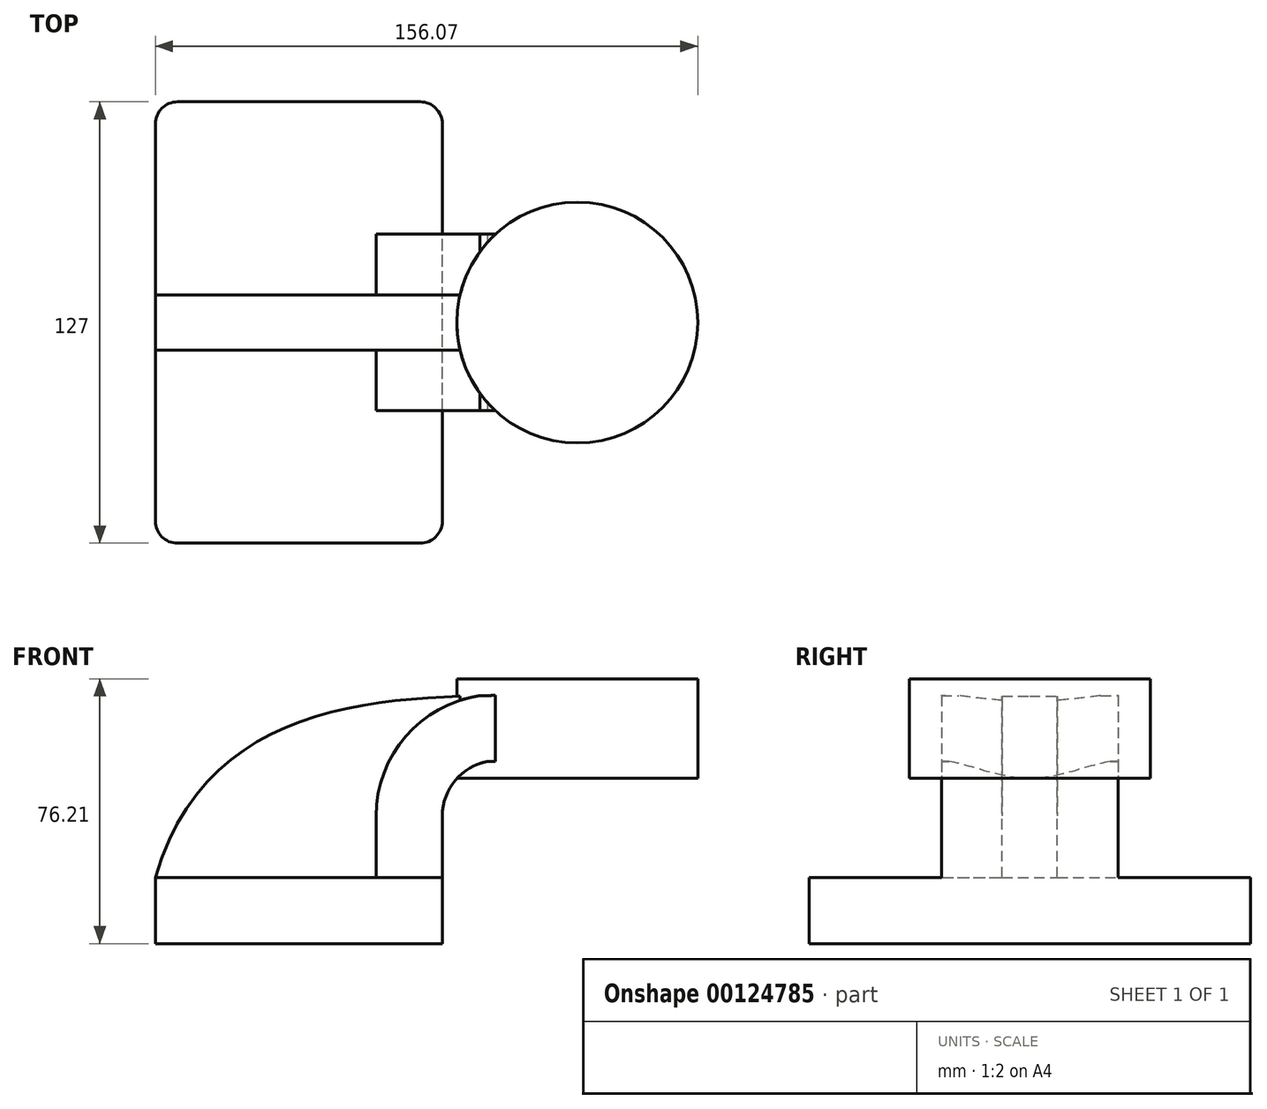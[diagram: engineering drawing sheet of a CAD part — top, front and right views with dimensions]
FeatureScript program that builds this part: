
annotation { "Feature Type Name" : "Feature", "Feature Type Description" : "" }
export const myFeature = defineFeature(function(context is Context, id is Id, definition is map)
    precondition{}
    {
        {
            var Q0;
            Q0=qCreatedBy(makeId("Front.planeOp"),FACE);
            var sketch = newSketch(context, id + "F0", { "sketchPlane" : qUnion([Q0])});
            skLineSegment(sketch, "E0.bottom", {"start": v(-41.28, 9.52) * mm, "end": v(41.28, 9.53) * mm});
            skLineSegment(sketch, "E0.top", {"start": v(-41.28, -9.53) * mm, "end": v(41.28, -9.53) * mm});
            skLineSegment(sketch, "E0.left", {"start": v(-41.28, 9.52) * mm, "end": v(-41.28, -9.53) * mm});
            skLineSegment(sketch, "E0.right", {"start": v(41.28, 9.53) * mm, "end": v(41.28, -9.52) * mm});
            skPoint(sketch, "E0.middle", {"position": v(0, 0) * mm});
            skLineSegment(sketch, "E1.bottom", {"start": v(64, 66.67) * mm, "end": v(114.8, 66.67) * mm});
            skLineSegment(sketch, "E1.top", {"start": v(64, 38.1) * mm, "end": v(114.8, 38.1) * mm});
            skLineSegment(sketch, "E1.left", {"start": v(64, 66.67) * mm, "end": v(64, 38.1) * mm});
            skLineSegment(sketch, "E1.right", {"start": v(114.8, 66.67) * mm, "end": v(114.8, 38.1) * mm});
            skPoint(sketch, "E1.middle", {"position": v(89.4, 52.39) * mm});
            skLineSegment(sketch, "E2", {"start": v(41.27, 9.53) * mm, "end": v(41.27, 27.25) * mm});
            skArc(sketch, "E3", {"start": v(41.27, 27.25) * mm, "mid": v(44.98, 37.44) * mm, "end": v(54.37, 42.88) * mm});
            skLineSegment(sketch, "E4", {"start": v(54.37, 42.88) * mm, "end": v(80.13, 42.88) * mm});
            skLineSegment(sketch, "E5.0", {"start": v(53.02, 61.93) * mm, "end": v(80.13, 61.93) * mm});
            skArc(sketch, "E5.1", {"start": v(22.22, 27.25) * mm, "mid": v(31.03, 50.43) * mm, "end": v(53.02, 61.93) * mm});
            skLineSegment(sketch, "E5.2", {"start": v(22.22, 9.53) * mm, "end": v(22.22, 27.25) * mm});
            skLineSegment(sketch, "E6", {"start": v(80.13, 38.1) * mm, "end": v(80.13, 66.67) * mm});
            skFitSpline(sketch, "E7", {"points": [v(-41.28, 9.52) * mm, v(64, 61.93) * mm], "startDerivative": vector(44.55, 155.05) * mm, "endDerivative": vector(115.8, 0.6) * mm});
            skSolve(sketch);
        }
        {
            var Q0;
            Q0=makeQuery(id+"F0.imprint","IMPRINT",FACE,{"disambiguationData":[TD([[makeQuery(id+"F0.imprint","IMPRINT",EDGE,{"derivedFrom":sQuery(id+"F0.wireOp",EDGE,"E0.top")}),1.0]])]});
            extrude(context, id + "F1", {"entities" : qUnion([Q0]), "endBound" : BoundingType.SYMMETRIC, "depth" : 127 * mm});
        }
        {
            var Q0;
            {var subQ1=sQuery(id+"F0.wireOp",EDGE,"E2");Q0=makeQuery(id+"F0.imprint","IMPRINT",FACE,{"disambiguationData":[TD([[makeQuery(id+"F0.imprint","IMPRINT",EDGE,{"derivedFrom":subQ1}),1.0]])]});}
            var Q1;
            {var subQ3=sQuery(id+"F0.wireOp",EDGE,"E4");var subQ5=sQuery(id+"F0.wireOp",EDGE,"E6");var subQ6=makeQuery(id+"F0.imprint","INTERSECT",VERTEX,{"derivedFrom":[subQ3,subQ5]});Q1=makeQuery(id+"F0.imprint","IMPRINT",FACE,{"disambiguationData":[TD([[makeQuery(id+"F0.imprint","IMPRINT",EDGE,{"disambiguationData":[TD([[subQ6,1.0]])],"derivedFrom":subQ3}),1.0]])]});}
            extrude(context, id + "F2", {"entities" : qUnion([Q0, Q1]), "operationType" : NewBodyOperationType.ADD, "endBound" : BoundingType.SYMMETRIC, "depth" : 50.8 * mm});
        }
        {
            var Q0;
            {var subQ3=sQuery(id+"F0.wireOp",EDGE,"E5.2");Q0=makeQuery(id+"F0.imprint","IMPRINT",FACE,{"disambiguationData":[TD([[makeQuery(id+"F0.imprint","IMPRINT",EDGE,{"derivedFrom":subQ3}),1.0]])]});}
            extrude(context, id + "F3", {"entities" : qUnion([Q0]), "operationType" : NewBodyOperationType.ADD, "endBound" : BoundingType.SYMMETRIC, "depth" : 15.88 * mm});
        }
        {
            var Q0;
            {var subQ0=sQuery(id+"F0.wireOp",EDGE,"E1.right");Q0=makeQuery(id+"F0.imprint","IMPRINT",FACE,{"disambiguationData":[TD([[makeQuery(id+"F0.imprint","IMPRINT",EDGE,{"derivedFrom":subQ0}),-1.0]])]});}
            var Q1;
            Q1=sQuery(id+"F0.wireOp",EDGE,"E6");
            revolve(context, id + "F4", {"operationType" : NewBodyOperationType.ADD, "entities" : qUnion([Q0]), "axis" : qUnion([Q1]), "revolveType" : RevolveType.FULL});
        }
        {
            var Q0;
            Q0=makeQuery(id+"F1.opExtrude","CAP_EDGE",EDGE,{"disambiguationData":[OSD([sQuery(id+"F0.wireOp",EDGE,"E0.right")])],"isStart":true});
            var Q1;
            Q1=makeQuery(id+"F1.opExtrude","CAP_EDGE",EDGE,{"disambiguationData":[OSD([sQuery(id+"F0.wireOp",EDGE,"E0.left")])],"isStart":true});
            var Q2;
            Q2=makeQuery(id+"F1.opExtrude","CAP_EDGE",EDGE,{"disambiguationData":[OSD([sQuery(id+"F0.wireOp",EDGE,"E0.left")])],"isStart":false});
            var Q3;
            Q3=makeQuery(id+"F1.opExtrude","CAP_EDGE",EDGE,{"disambiguationData":[OSD([sQuery(id+"F0.wireOp",EDGE,"E0.right")])],"isStart":false});
            fillet(context, id + "F5", {"entities" : qUnion([Q0, Q1, Q2, Q3]), "radius" : 6.35 * mm, "tangentPropagation" : true, "allowEdgeOverflow" : false});
        }
    });
